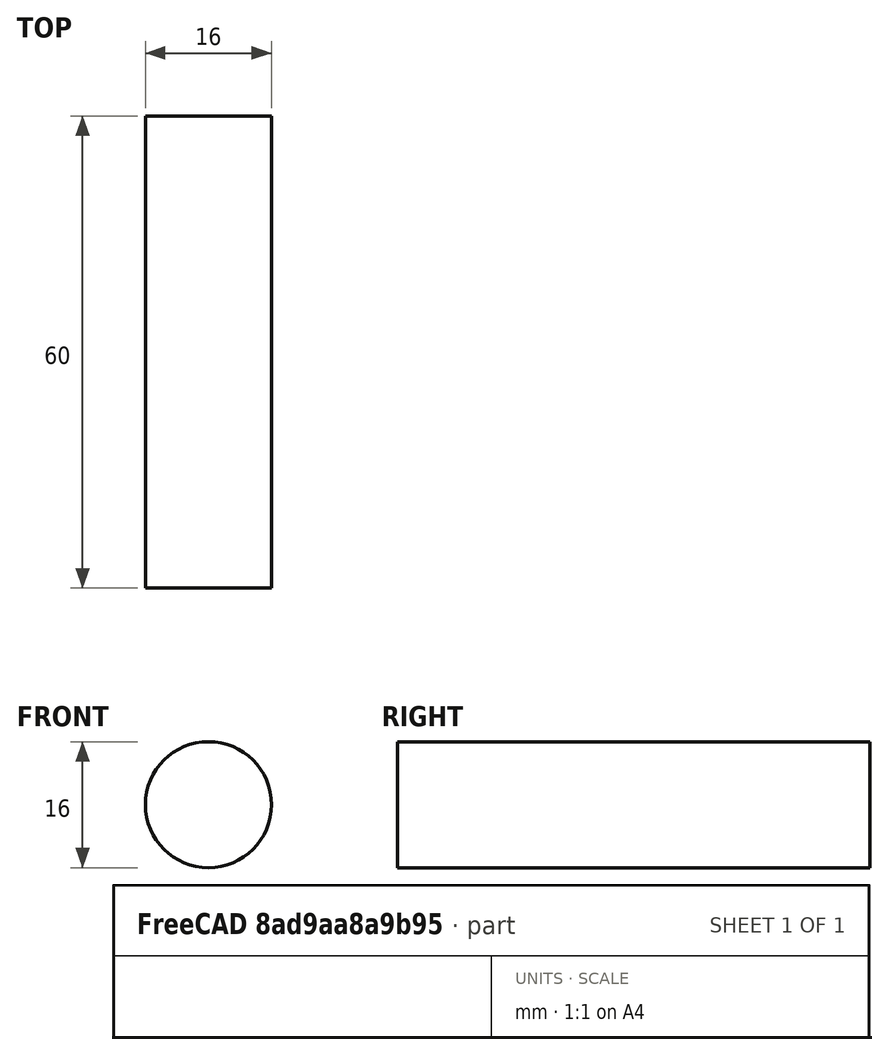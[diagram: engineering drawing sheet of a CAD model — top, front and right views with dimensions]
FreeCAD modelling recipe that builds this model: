
FCSTD DOCUMENT  (FreeCAD 0.17R13510 +12 (Git))
Label: octane
License: All rights reserved
LicenseURL: http://en.wikipedia.org/wiki/All_rights_reserved
objects: Mesh::Feature×2, Part::Cylinder×1, Spreadsheet::Sheet×1
note: 1 computed .brp shape members not serialized (recipe doc carries the construction recipe); baked Part::Feature solids carry a one-line shape summary decoded from their .brp

FEATURE [Mesh::Feature] Octane_B
FEATURE [Mesh::Feature] Octane_U
FEATURE [Part::Cylinder] Cylinder  label="Zylinder"
  Angle = 360
  AttacherType = Attacher::AttachEngine3D
  Height = 60
  Placement = pos=(-35,30,-4) rot=(1,0,0;1.5708rad)
  Radius = 8
  expr: Placement.Base.z = Spreadsheet.z_off_rear
  expr: Placement.Base.y = Spreadsheet.y_off_rear
  expr: Radius = Spreadsheet.inner_r + Spreadsheet.thickness
  expr: Placement.Base.x = Spreadsheet.x_off_rear
  expr: Height = Spreadsheet.height_rear
FEATURE [Spreadsheet::Sheet] Spreadsheet
  cells = A1=height_front; B1(height_front)=10; A2=height_rear; B2(height_rear)=60; A3=inner_r; B3(inner_r)=6; A4=thickness; B4(thickness)=2; A5=x_off_rear; B5(x_off_rear)=-35; A6=x_off_front; B6(x_off_front)=20; A7=y_off_rear; B7(y_off_rear)=30; A8=y_off_front; B8(y_off_front)=2; A9=z_off_front; B9(z_off_front)=1; A10=z_off_rear; B10(z_off_rear)=-4
